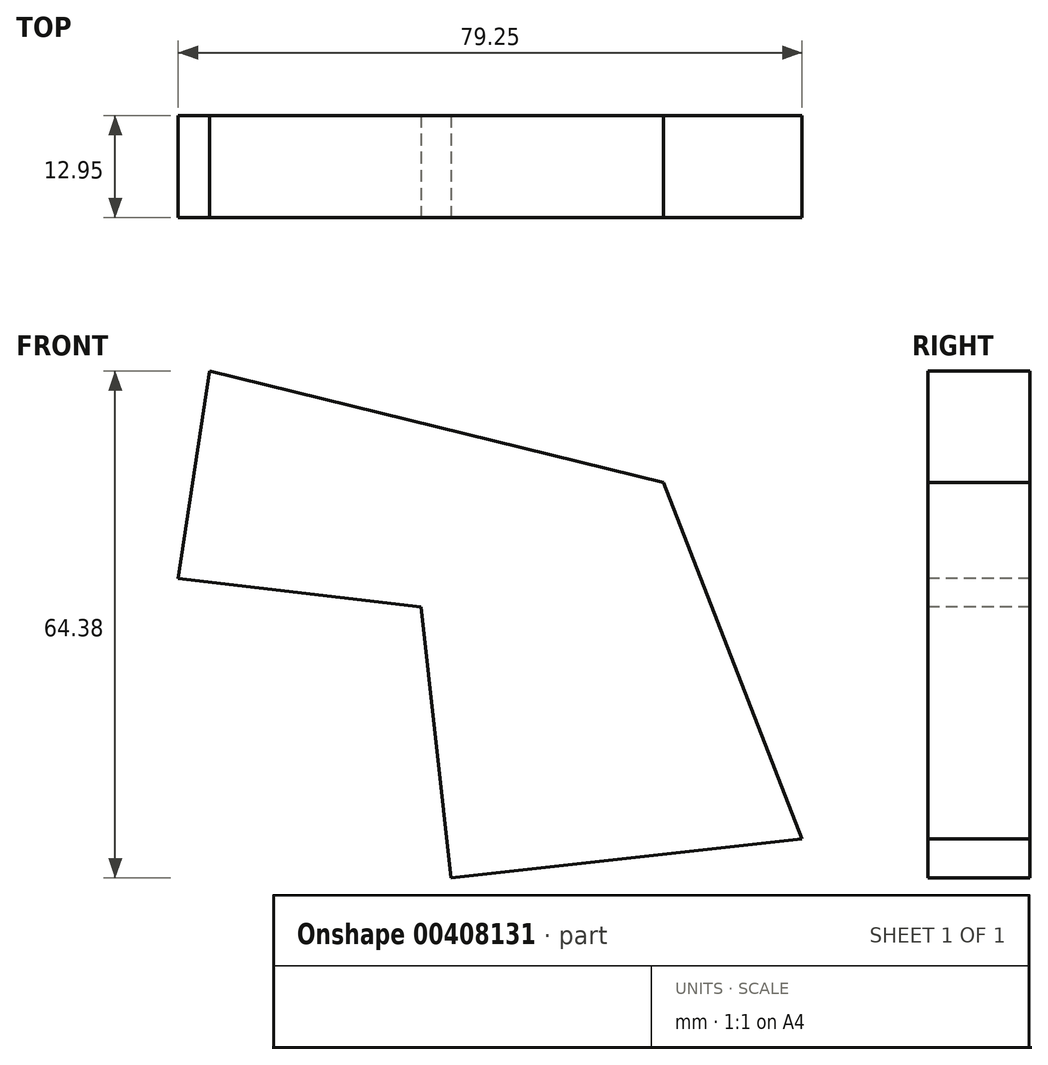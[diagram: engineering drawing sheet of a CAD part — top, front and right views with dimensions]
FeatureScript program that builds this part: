
annotation { "Feature Type Name" : "Feature", "Feature Type Description" : "" }
export const myFeature = defineFeature(function(context is Context, id is Id, definition is map)
    precondition{}
    {
        {
            var Q0;
            Q0=qCreatedBy(makeId("Front.planeOp"),FACE);
            var sketch = newSketch(context, id + "F0", { "sketchPlane" : qUnion([Q0])});
            skLineSegment(sketch, "E0", {"start": v(-35.1, 32.12) * mm, "end": v(22.58, 17.97) * mm});
            skLineSegment(sketch, "E1", {"start": v(22.58, 17.97) * mm, "end": v(40.2, -27.29) * mm});
            skLineSegment(sketch, "E2", {"start": v(40.2, -27.29) * mm, "end": v(-4.38, -32.26) * mm});
            skLineSegment(sketch, "E3", {"start": v(-4.38, -32.26) * mm, "end": v(-8.22, 2.17) * mm});
            skLineSegment(sketch, "E4", {"start": v(-8.22, 2.17) * mm, "end": v(-39.05, 5.8) * mm});
            skLineSegment(sketch, "E5", {"start": v(-39.05, 5.8) * mm, "end": v(-35.1, 32.12) * mm});
            skSolve(sketch);
        }
        {
            var Q0;
            Q0 = qSketchRegion(id + "F0", true);
            extrude(context, id + "F1", {"entities" : qUnion([Q0]), "oppositeDirection" : true, "depth" : 12.95 * mm});
        }
        {
            var Q0;
            Q0=makeQuery(id+"F1.opExtrude","CAP_FACE",FACE,{"disambiguationData":[OSD([sQuery(id+"F0.wireOp",EDGE,"E0"),sQuery(id+"F0.wireOp",EDGE,"E1"),sQuery(id+"F0.wireOp",EDGE,"E2"),sQuery(id+"F0.wireOp",EDGE,"E3"),sQuery(id+"F0.wireOp",EDGE,"E4"),sQuery(id+"F0.wireOp",EDGE,"E5")])],"isStart":false});
            var sketch = newSketch(context, id + "F2", { "sketchPlane" : qUnion([Q0])});
            skCircle(sketch, "E6", {"center": v(-14.08, 2.17) * mm, "radius": 10.5 * mm});
            skSolve(sketch);
        }
        {
            var Q0;
            Q0=makeQuery(id+"F2.imprint","IMPRINT",FACE,{"disambiguationData":[TD([[makeQuery(id+"F2.imprint","IMPRINT",EDGE,{"derivedFrom":sQuery(id+"F2.wireOp",EDGE,"E6")}),1.0]])]});
            extrude(context, id + "F3", {"entities" : qUnion([Q0]), "operationType" : NewBodyOperationType.ADD, "oppositeDirection" : true, "depth" : 10.67 * mm});
        }
    });
